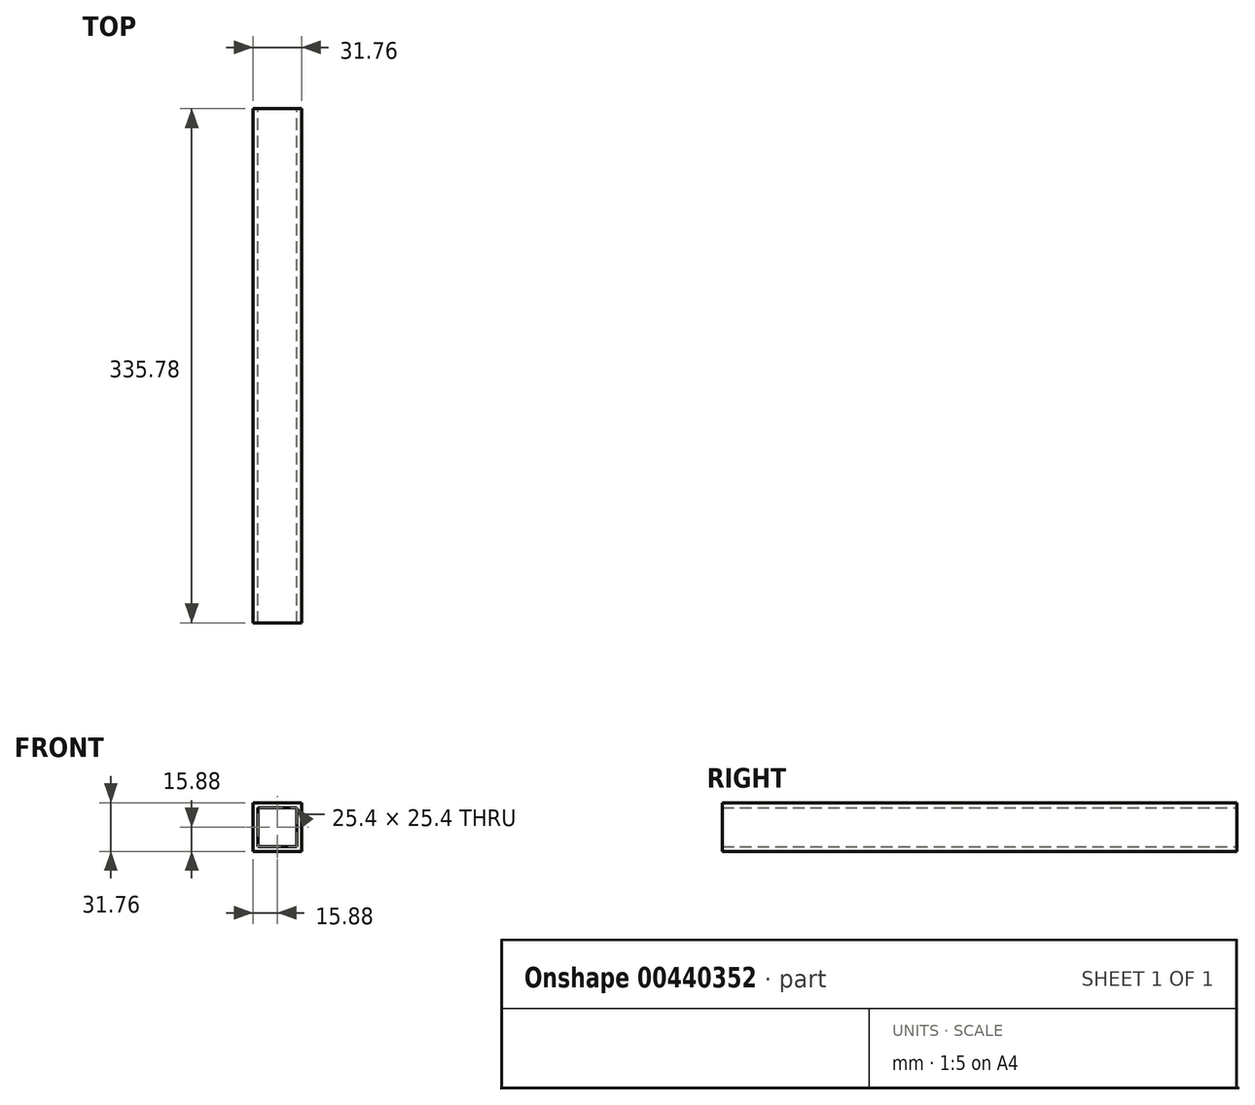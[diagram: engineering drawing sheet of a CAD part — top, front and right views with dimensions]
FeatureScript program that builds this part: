
annotation { "Feature Type Name" : "Feature", "Feature Type Description" : "" }
export const myFeature = defineFeature(function(context is Context, id is Id, definition is map)
    precondition{}
    {
        {
            var Q0;
            Q0=qCreatedBy(makeId("Front.planeOp"),FACE);
            var sketch = newSketch(context, id + "F0", { "sketchPlane" : qUnion([Q0])});
            skLineSegment(sketch, "E0.bottom", {"start": v(-15.88, 15.88) * mm, "end": v(15.88, 15.88) * mm});
            skLineSegment(sketch, "E0.top", {"start": v(-15.88, -15.88) * mm, "end": v(15.88, -15.88) * mm});
            skLineSegment(sketch, "E0.left", {"start": v(-15.88, 15.88) * mm, "end": v(-15.88, -15.88) * mm});
            skLineSegment(sketch, "E0.right", {"start": v(15.88, 15.88) * mm, "end": v(15.88, -15.88) * mm});
            skPoint(sketch, "E0.middle", {"position": v(0, 0) * mm});
            skLineSegment(sketch, "E1.bottom", {"start": v(-12.7, 12.7) * mm, "end": v(12.7, 12.7) * mm});
            skLineSegment(sketch, "E1.top", {"start": v(-12.7, -12.7) * mm, "end": v(12.7, -12.7) * mm});
            skLineSegment(sketch, "E1.left", {"start": v(-12.7, 12.7) * mm, "end": v(-12.7, -12.7) * mm});
            skLineSegment(sketch, "E1.right", {"start": v(12.7, 12.7) * mm, "end": v(12.7, -12.7) * mm});
            skSolve(sketch);
        }
        {
            var Q0;
            Q0=makeQuery(id+"F0.imprint","IMPRINT",FACE,{"disambiguationData":[TD([[makeQuery(id+"F0.imprint","IMPRINT",EDGE,{"derivedFrom":sQuery(id+"F0.wireOp",EDGE,"E0.bottom")}),-1.0]])]});
            extrude(context, id + "F1", {"entities" : qUnion([Q0]), "endBound" : BoundingType.SYMMETRIC, "depth" : 335.8 * mm});
        }
    });
